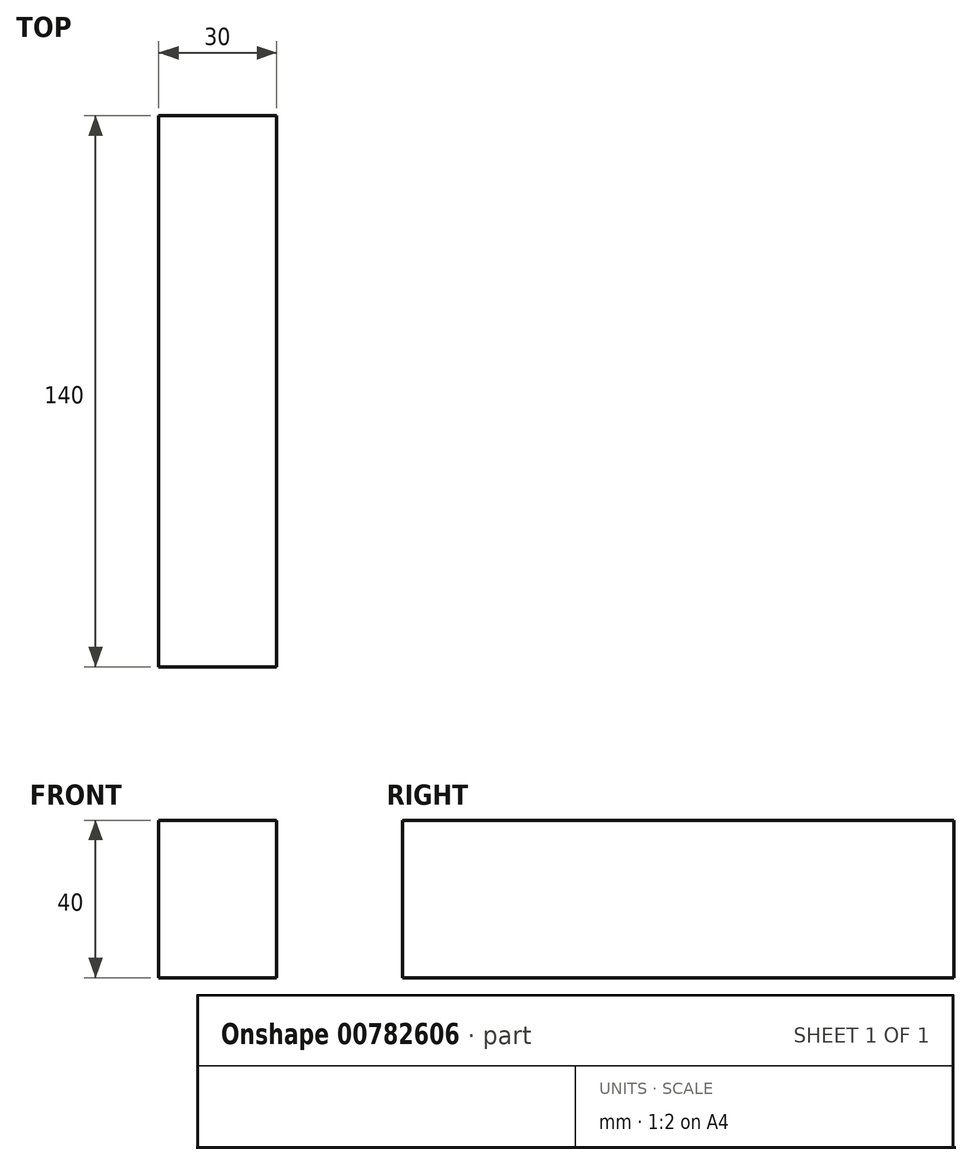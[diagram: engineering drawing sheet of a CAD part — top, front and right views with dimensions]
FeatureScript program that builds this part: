
annotation { "Feature Type Name" : "Feature", "Feature Type Description" : "" }
export const myFeature = defineFeature(function(context is Context, id is Id, definition is map)
    precondition{}
    {
        {
            var Q0;
            Q0=qCreatedBy(makeId("Top.planeOp"),FACE);
            var sketch = newSketch(context, id + "F0", { "sketchPlane" : qUnion([Q0])});
            skLineSegment(sketch, "E0.bottom", {"start": v(15, -70) * mm, "end": v(-15, -70) * mm});
            skLineSegment(sketch, "E0.top", {"start": v(15, 70) * mm, "end": v(-15, 70) * mm});
            skLineSegment(sketch, "E0.left", {"start": v(15, -70) * mm, "end": v(15, 70) * mm});
            skLineSegment(sketch, "E0.right", {"start": v(-15, -70) * mm, "end": v(-15, 70) * mm});
            skPoint(sketch, "E0.middle", {"position": v(0, 0) * mm});
            skSolve(sketch);
        }
        {
            var Q0;
            Q0 = qSketchRegion(id + "F0", true);
            extrude(context, id + "F1", {"entities" : qUnion([Q0]), "depth" : 40 * mm, "offsetDistance" : 25 * mm});
        }
    });
